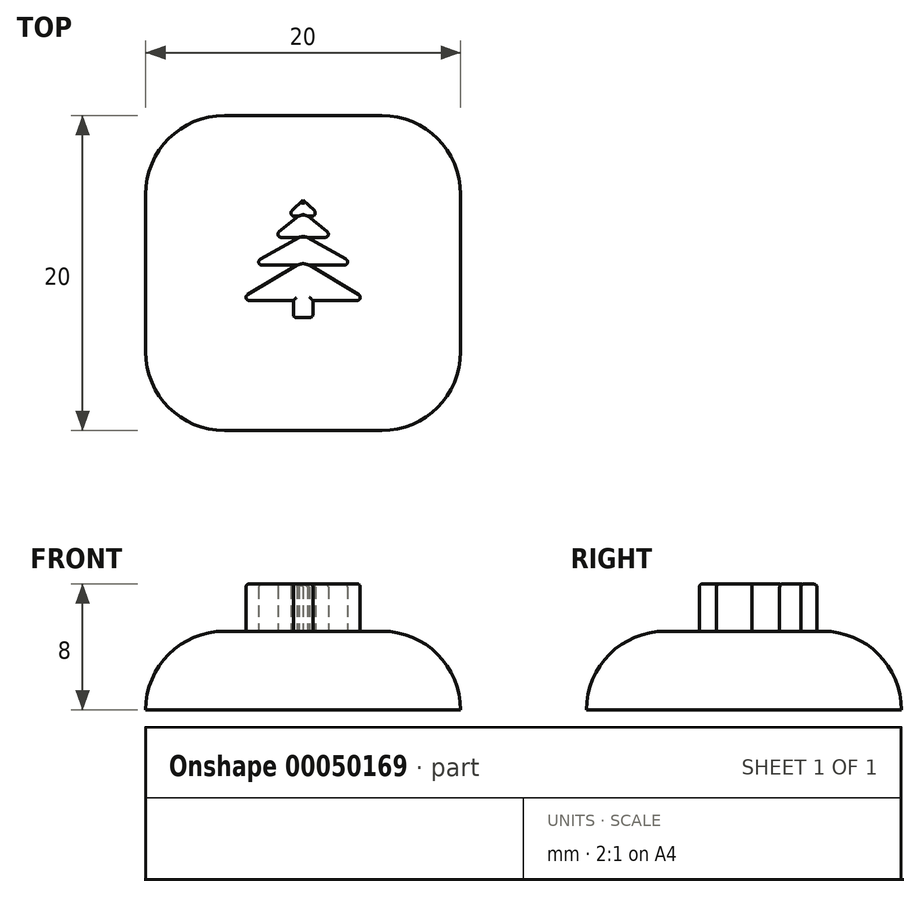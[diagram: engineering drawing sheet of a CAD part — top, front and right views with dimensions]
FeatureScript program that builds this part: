
annotation { "Feature Type Name" : "Feature", "Feature Type Description" : "" }
export const myFeature = defineFeature(function(context is Context, id is Id, definition is map)
    precondition{}
    {
        {
            var Q0;
            Q0=qCreatedBy(makeId("Top.planeOp"),FACE);
            var sketch = newSketch(context, id + "F0", { "sketchPlane" : qUnion([Q0])});
            skLineSegment(sketch, "E0.rect.bottom", {"start": v(10, -10) * mm, "end": v(-10, -10) * mm});
            skLineSegment(sketch, "E0.rect.top", {"start": v(10, 10) * mm, "end": v(-10, 10) * mm});
            skLineSegment(sketch, "E0.rect.left", {"start": v(10, -10) * mm, "end": v(10, 10) * mm});
            skLineSegment(sketch, "E0.rect.right", {"start": v(-10, -10) * mm, "end": v(-10, 10) * mm});
            skPoint(sketch, "E0.rect.middle", {"position": v(0, 0) * mm});
            skSolve(sketch);
        }
        {
            var Q0;
            Q0 = qSketchRegion(id + "F0", true);
            extrude(context, id + "F1", {"entities" : qUnion([Q0]), "oppositeDirection" : true, "depth" : 5 * mm});
        }
        {
            var Q0;
            Q0=makeQuery(id+"F1.opExtrude","CAP_EDGE",EDGE,{"disambiguationData":[OSD([sQuery(id+"F0.wireOp",EDGE,"E0.rect.top")])],"isStart":true});
            var Q1;
            Q1=makeQuery(id+"F1.opExtrude","CAP_EDGE",EDGE,{"disambiguationData":[OSD([sQuery(id+"F0.wireOp",EDGE,"E0.rect.right")])],"isStart":true});
            var Q2;
            Q2=makeQuery(id+"F1.opExtrude","CAP_EDGE",EDGE,{"disambiguationData":[OSD([sQuery(id+"F0.wireOp",EDGE,"E0.rect.bottom")])],"isStart":true});
            var Q3;
            Q3=makeQuery(id+"F1.opExtrude","CAP_EDGE",EDGE,{"disambiguationData":[OSD([sQuery(id+"F0.wireOp",EDGE,"E0.rect.left")])],"isStart":true});
            fillet(context, id + "F2", {"entities" : qUnion([Q0, Q1, Q2, Q3]), "radius" : 5 * mm, "tangentPropagation" : true, "allowEdgeOverflow" : false});
        }
        {
            var Q0;
            Q0=makeQuery(id+"F2.opFillet","BLEND_EDGE",EDGE,{"blendedFrom":[makeQuery(id+"F1.opExtrude","CAP_EDGE",EDGE,{"disambiguationData":[OSD([sQuery(id+"F0.wireOp",EDGE,"E0.rect.top")])],"isStart":true}),makeQuery(id+"F1.opExtrude","CAP_EDGE",EDGE,{"disambiguationData":[OSD([sQuery(id+"F0.wireOp",EDGE,"E0.rect.right")])],"isStart":true})],"blendedInto":[]});
            var Q1;
            Q1=makeQuery(id+"F2.opFillet","BLEND_EDGE",EDGE,{"blendedFrom":[makeQuery(id+"F1.opExtrude","CAP_EDGE",EDGE,{"disambiguationData":[OSD([sQuery(id+"F0.wireOp",EDGE,"E0.rect.top")])],"isStart":true}),makeQuery(id+"F1.opExtrude","CAP_EDGE",EDGE,{"disambiguationData":[OSD([sQuery(id+"F0.wireOp",EDGE,"E0.rect.left")])],"isStart":true})],"blendedInto":[]});
            var Q2;
            Q2=makeQuery(id+"F2.opFillet","BLEND_EDGE",EDGE,{"blendedFrom":[makeQuery(id+"F1.opExtrude","CAP_EDGE",EDGE,{"disambiguationData":[OSD([sQuery(id+"F0.wireOp",EDGE,"E0.rect.bottom")])],"isStart":true}),makeQuery(id+"F1.opExtrude","CAP_EDGE",EDGE,{"disambiguationData":[OSD([sQuery(id+"F0.wireOp",EDGE,"E0.rect.left")])],"isStart":true})],"blendedInto":[]});
            var Q3;
            {var subQ0=sQuery(id+"F0.wireOp",EDGE,"E0.rect.right");Q3=makeQuery(id+"F2.opFillet","BLEND_EDGE",EDGE,{"blendedFrom":[makeQuery(id+"F1.opExtrude","CAP_EDGE",EDGE,{"disambiguationData":[OSD([subQ0])],"isStart":true}),makeQuery(id+"F1.opExtrude","CAP_FACE",FACE,{"disambiguationData":[OSD([sQuery(id+"F0.wireOp",EDGE,"E0.rect.bottom"),sQuery(id+"F0.wireOp",EDGE,"E0.rect.top"),sQuery(id+"F0.wireOp",EDGE,"E0.rect.left"),subQ0])],"isStart":true})],"blendedInto":[makeQuery(id+"F1.opExtrude","CAP_FACE",FACE,{"disambiguationData":[OSD([sQuery(id+"F0.wireOp",EDGE,"E0.rect.bottom"),sQuery(id+"F0.wireOp",EDGE,"E0.rect.top"),sQuery(id+"F0.wireOp",EDGE,"E0.rect.left"),subQ0])],"isStart":true})]});}
            var Q4;
            Q4=makeQuery(id+"F2.opFillet","BLEND_EDGE",EDGE,{"blendedFrom":[makeQuery(id+"F1.opExtrude","CAP_EDGE",EDGE,{"disambiguationData":[OSD([sQuery(id+"F0.wireOp",EDGE,"E0.rect.bottom")])],"isStart":true}),makeQuery(id+"F1.opExtrude","CAP_EDGE",EDGE,{"disambiguationData":[OSD([sQuery(id+"F0.wireOp",EDGE,"E0.rect.right")])],"isStart":true})],"blendedInto":[]});
            fillet(context, id + "F3", {"entities" : qUnion([Q0, Q1, Q2, Q3, Q4]), "radius" : 5 * mm, "tangentPropagation" : true, "allowEdgeOverflow" : false});
        }
        {
            var Q0;
            Q0=makeQuery(id+"F1.opExtrude","CAP_FACE",FACE,{"disambiguationData":[OSD([sQuery(id+"F0.wireOp",EDGE,"E0.rect.bottom"),sQuery(id+"F0.wireOp",EDGE,"E0.rect.top"),sQuery(id+"F0.wireOp",EDGE,"E0.rect.left"),sQuery(id+"F0.wireOp",EDGE,"E0.rect.right")])],"isStart":true});
            var sketch = newSketch(context, id + "F4", { "sketchPlane" : qUnion([Q0])});
            skLineSegment(sketch, "E1", {"start": v(0, 4.64) * mm, "end": v(0, -3.83) * mm, "construction": true});
            skLineSegment(sketch, "E2", {"start": v(0, 4.64) * mm, "end": v(-1.07, 3.61) * mm});
            skLineSegment(sketch, "E3", {"start": v(-1.07, 3.61) * mm, "end": v(-0.3, 3.61) * mm});
            skLineSegment(sketch, "E4", {"start": v(-0.3, 3.61) * mm, "end": v(-1.97, 2.27) * mm});
            skLineSegment(sketch, "E5", {"start": v(-1.97, 2.27) * mm, "end": v(-0.27, 2.27) * mm});
            skLineSegment(sketch, "E6", {"start": v(-0.27, 2.27) * mm, "end": v(-3.38, 0.5) * mm});
            skLineSegment(sketch, "E7", {"start": v(-3.38, 0.5) * mm, "end": v(-0.4, 0.5) * mm});
            skLineSegment(sketch, "E8", {"start": v(-0.4, 0.5) * mm, "end": v(-4.15, -1.75) * mm});
            skLineSegment(sketch, "E9", {"start": v(-4.15, -1.75) * mm, "end": v(-0.62, -1.75) * mm});
            skLineSegment(sketch, "E10", {"start": v(-0.62, -1.75) * mm, "end": v(-0.62, -2.84) * mm});
            skLineSegment(sketch, "E11", {"start": v(-0.62, -2.84) * mm, "end": v(0, -2.84) * mm});
            skLineSegment(sketch, "E12.MirrorCS", {"start": v(0, 4.64) * mm, "end": v(1.07, 3.61) * mm});
            skLineSegment(sketch, "E13.MirrorCS", {"start": v(0.3, 3.61) * mm, "end": v(1.97, 2.27) * mm});
            skLineSegment(sketch, "E14.MirrorCS", {"start": v(1.07, 3.61) * mm, "end": v(0.3, 3.61) * mm});
            skLineSegment(sketch, "E15.MirrorCS", {"start": v(0.27, 2.27) * mm, "end": v(3.38, 0.5) * mm});
            skLineSegment(sketch, "E16.MirrorCS", {"start": v(1.97, 2.27) * mm, "end": v(0.27, 2.27) * mm});
            skLineSegment(sketch, "E17.MirrorCS", {"start": v(3.38, 0.5) * mm, "end": v(0.4, 0.5) * mm});
            skLineSegment(sketch, "E18.MirrorCS", {"start": v(0.4, 0.5) * mm, "end": v(4.15, -1.75) * mm});
            skLineSegment(sketch, "E19.MirrorCS", {"start": v(4.15, -1.75) * mm, "end": v(0.62, -1.75) * mm});
            skLineSegment(sketch, "E20.MirrorCS", {"start": v(0.62, -1.75) * mm, "end": v(0.62, -2.84) * mm});
            skLineSegment(sketch, "E21.MirrorCS", {"start": v(0.62, -2.84) * mm, "end": v(0, -2.84) * mm});
            skSolve(sketch);
        }
        {
            var Q0;
            Q0 = qSketchRegion(id + "F4", true);
            extrude(context, id + "F5", {"entities" : qUnion([Q0]), "operationType" : NewBodyOperationType.ADD, "depth" : 3 * mm});
        }
        {
            var Q0;
            Q0=makeQuery(id+"F5.opExtrude","CAP_EDGE",EDGE,{"disambiguationData":[OSD([sQuery(id+"F4.wireOp",EDGE,"E5")])],"isStart":false});
            var Q1;
            Q1=makeQuery(id+"F5.opExtrude","CAP_EDGE",EDGE,{"disambiguationData":[OSD([sQuery(id+"F4.wireOp",EDGE,"E3")])],"isStart":false});
            var Q2;
            Q2=makeQuery(id+"F5.opExtrude","CAP_EDGE",EDGE,{"disambiguationData":[OSD([sQuery(id+"F4.wireOp",EDGE,"E14.MirrorCS")])],"isStart":false});
            var Q3;
            Q3=makeQuery(id+"F5.opExtrude","CAP_EDGE",EDGE,{"disambiguationData":[OSD([sQuery(id+"F4.wireOp",EDGE,"E16.MirrorCS")])],"isStart":false});
            var Q4;
            Q4=makeQuery(id+"F5.opExtrude","CAP_EDGE",EDGE,{"disambiguationData":[OSD([sQuery(id+"F4.wireOp",EDGE,"E17.MirrorCS")])],"isStart":false});
            var Q5;
            Q5=makeQuery(id+"F5.opExtrude","CAP_EDGE",EDGE,{"disambiguationData":[OSD([sQuery(id+"F4.wireOp",EDGE,"E7")])],"isStart":false});
            var Q6;
            Q6=makeQuery(id+"F5.opExtrude","CAP_EDGE",EDGE,{"disambiguationData":[OSD([sQuery(id+"F4.wireOp",EDGE,"E9")])],"isStart":false});
            var Q7;
            Q7=makeQuery(id+"F5.opExtrude","CAP_EDGE",EDGE,{"disambiguationData":[OSD([sQuery(id+"F4.wireOp",EDGE,"E19.MirrorCS")])],"isStart":false});
            var Q8;
            Q8=makeQuery(id+"F5.opExtrude","CAP_EDGE",EDGE,{"disambiguationData":[OSD([sQuery(id+"F4.wireOp",EDGE,"E11"),sQuery(id+"F4.wireOp",EDGE,"E21.MirrorCS")])],"isStart":false});
            var Q9;
            Q9=makeQuery(id+"F5.opExtrude","CAP_EDGE",EDGE,{"disambiguationData":[OSD([sQuery(id+"F4.wireOp",EDGE,"E10")])],"isStart":false});
            var Q10;
            Q10=makeQuery(id+"F5.opExtrude","CAP_EDGE",EDGE,{"disambiguationData":[OSD([sQuery(id+"F4.wireOp",EDGE,"E20.MirrorCS")])],"isStart":false});
            var Q11;
            Q11=makeQuery(id+"F5.opExtrude","CAP_EDGE",EDGE,{"disambiguationData":[OSD([sQuery(id+"F4.wireOp",EDGE,"E18.MirrorCS")])],"isStart":false});
            var Q12;
            Q12=makeQuery(id+"F5.opExtrude","CAP_EDGE",EDGE,{"disambiguationData":[OSD([sQuery(id+"F4.wireOp",EDGE,"E8")])],"isStart":false});
            var Q13;
            Q13=makeQuery(id+"F5.opExtrude","CAP_EDGE",EDGE,{"disambiguationData":[OSD([sQuery(id+"F4.wireOp",EDGE,"E6")])],"isStart":false});
            var Q14;
            Q14=makeQuery(id+"F5.opExtrude","CAP_EDGE",EDGE,{"disambiguationData":[OSD([sQuery(id+"F4.wireOp",EDGE,"E15.MirrorCS")])],"isStart":false});
            var Q15;
            Q15=makeQuery(id+"F5.opExtrude","CAP_EDGE",EDGE,{"disambiguationData":[OSD([sQuery(id+"F4.wireOp",EDGE,"E13.MirrorCS")])],"isStart":false});
            var Q16;
            Q16=makeQuery(id+"F5.opExtrude","CAP_EDGE",EDGE,{"disambiguationData":[OSD([sQuery(id+"F4.wireOp",EDGE,"E4")])],"isStart":false});
            var Q17;
            Q17=makeQuery(id+"F5.opExtrude","CAP_EDGE",EDGE,{"disambiguationData":[OSD([sQuery(id+"F4.wireOp",EDGE,"E12.MirrorCS")])],"isStart":false});
            var Q18;
            Q18=makeQuery(id+"F5.opExtrude","CAP_EDGE",EDGE,{"disambiguationData":[OSD([sQuery(id+"F4.wireOp",EDGE,"E2")])],"isStart":false});
            fillet(context, id + "F6", {"entities" : qUnion([Q0, Q1, Q2, Q3, Q4, Q5, Q6, Q7, Q8, Q9, Q10, Q11, Q12, Q13, Q14, Q15, Q16, Q17, Q18]), "radius" : 0.2 * mm, "tangentPropagation" : true, "allowEdgeOverflow" : false});
        }
        {
            var Q0;
            Q0=makeQuery(id+"F5.opExtrude","SWEPT_EDGE",EDGE,{"disambiguationData":[OSD([sQuery(id+"F4.wireOp",EDGE,"E12.MirrorCS"),sQuery(id+"F4.wireOp",EDGE,"E14.MirrorCS")])]});
            var Q1;
            Q1=makeQuery(id+"F5.opExtrude","SWEPT_EDGE",EDGE,{"disambiguationData":[OSD([sQuery(id+"F4.wireOp",EDGE,"E13.MirrorCS"),sQuery(id+"F4.wireOp",EDGE,"E16.MirrorCS")])]});
            var Q2;
            Q2=makeQuery(id+"F5.opExtrude","SWEPT_EDGE",EDGE,{"disambiguationData":[OSD([sQuery(id+"F4.wireOp",EDGE,"E15.MirrorCS"),sQuery(id+"F4.wireOp",EDGE,"E17.MirrorCS")])]});
            var Q3;
            Q3=makeQuery(id+"F5.opExtrude","SWEPT_EDGE",EDGE,{"disambiguationData":[OSD([sQuery(id+"F4.wireOp",EDGE,"E18.MirrorCS"),sQuery(id+"F4.wireOp",EDGE,"E19.MirrorCS")])]});
            var Q4;
            Q4=makeQuery(id+"F5.opExtrude","SWEPT_EDGE",EDGE,{"disambiguationData":[OSD([sQuery(id+"F4.wireOp",EDGE,"E20.MirrorCS"),sQuery(id+"F4.wireOp",EDGE,"E21.MirrorCS")])]});
            var Q5;
            Q5=makeQuery(id+"F5.opExtrude","SWEPT_EDGE",EDGE,{"disambiguationData":[OSD([sQuery(id+"F4.wireOp",EDGE,"E10"),sQuery(id+"F4.wireOp",EDGE,"E11")])]});
            var Q6;
            Q6=makeQuery(id+"F5.opExtrude","SWEPT_EDGE",EDGE,{"disambiguationData":[OSD([sQuery(id+"F4.wireOp",EDGE,"E6"),sQuery(id+"F4.wireOp",EDGE,"E7")])]});
            var Q7;
            Q7=makeQuery(id+"F5.opExtrude","SWEPT_EDGE",EDGE,{"disambiguationData":[OSD([sQuery(id+"F4.wireOp",EDGE,"E4"),sQuery(id+"F4.wireOp",EDGE,"E5")])]});
            var Q8;
            Q8=makeQuery(id+"F5.opExtrude","SWEPT_EDGE",EDGE,{"disambiguationData":[OSD([sQuery(id+"F4.wireOp",EDGE,"E2"),sQuery(id+"F4.wireOp",EDGE,"E3")])]});
            var Q9;
            Q9=makeQuery(id+"F5.opExtrude","SWEPT_EDGE",EDGE,{"disambiguationData":[OSD([sQuery(id+"F4.wireOp",EDGE,"E8"),sQuery(id+"F4.wireOp",EDGE,"E9")])]});
            fillet(context, id + "F7", {"entities" : qUnion([Q0, Q1, Q2, Q3, Q4, Q5, Q6, Q7, Q8, Q9]), "radius" : 0.2 * mm, "tangentPropagation" : true, "allowEdgeOverflow" : false});
        }
    });
